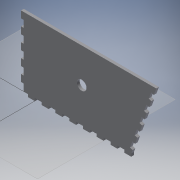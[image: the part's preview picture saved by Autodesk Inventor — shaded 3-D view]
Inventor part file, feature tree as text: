
AUTODESK INVENTOR PART (.ipt)
format: ipt  version: 2019 (Build 230136000, 136)  size: 210,944 bytes
history: native  units: mm
features: reference x9, other x4, extrude x3, sketch x3
ambient origin geometry x8: Origin, YZ Plane, XZ Plane, XY Plane, X Axis, Y Axis, Z Axis, Center Point
bodies: Body1 (feature_tree)
feature tree (19):
  other  "Твердое тело1"
  extrude  "Выдавливание1"  Depth=100.0mm
  extrude  "Выдавливание2"  Depth=12.217305mm
  extrude  "Выдавливание3"  Depth=4.0mm
  sketch  "Эскиз1"
  reference  "Ссылка1"
  reference  "Ссылка2"
  reference  "Ссылка3"
  reference  "Ссылка4"
  reference  "Ссылка5"
  reference  "Ссылка6"
  reference  "Ссылка7"
  reference  "Ссылка8"
  reference  "Ссылка9"
  sketch  "Эскиз2"
  sketch  "Эскиз3"
  parser-record x1  (decoder bookkeeping rows leaked as tree rows — omitted from the tree; the rows remain in map.json)
  other  "kowsh.iam"
  other  "Stenka:1"
note: 1 file-system path scrubbed to <path> (originals preserved in map.json)
